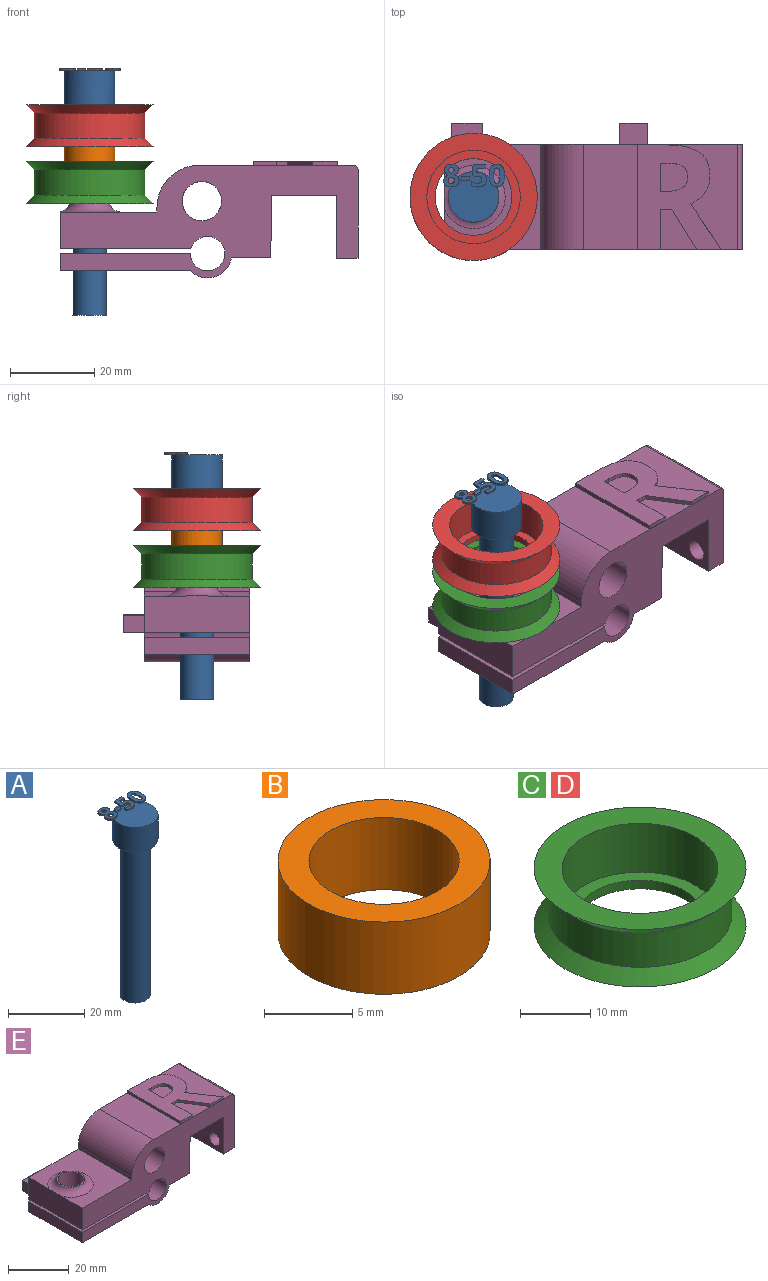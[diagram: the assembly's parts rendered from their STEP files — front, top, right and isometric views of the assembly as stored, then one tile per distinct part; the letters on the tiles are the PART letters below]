
ASSEMBLY  parts=5 mates=4
PART A: 86 faces, bbox 14.5x13.7x58.5 mm
  f0: plane 12x12mm, normal (0,0,1), area 99.4mm2, adj f5,f22,f23,f24,f25,f26,f40,f41
  f1: plane 1x0.26mm, normal (0,0,1), area 0.1mm2, adj f5,f46,f47,f48,f49
  f2: plane 0.85x0.68mm, normal (0,0,1), area 0.2mm2, adj f5,f29,f30,f31
  f3: cylinder r=4mm len=50mm, axis (0,0,-1), area 1256.6mm2, adj f4,f6
  f4: plane 8x8mm, normal (0,0,-1), area 50.3mm2, adj f3
  f5: cylinder r=6mm len=12mm, axis (0,0,-1), area 301.6mm2, adj f0,f1,f2,f6,f39,f45,f67,f85
  f6: plane 12x12mm, normal (0,0,-1), area 62.8mm2, adj f3,f5
  f7: extruded ~0.5x0.46mm, area 0.2mm2, adj f8,f37,f38,f39
  f8: extruded ~0.5x0.46mm, area 0.2mm2, adj f7,f9,f38,f39
  f9: extruded ~0.5x0.39mm, area 0.2mm2, adj f8,f10,f38,f39
  f10: extruded ~0.5x0.4mm, area 0.2mm2, adj f9,f11,f38,f39
  f11: extruded ~0.5x0.49mm, area 0.3mm2, adj f10,f12,f38,f39
  f12: extruded ~0.5x0.5mm, area 0.3mm2, adj f11,f13,f38,f39
  f13: extruded ~0.5x0.39mm, area 0.2mm2, adj f12,f37,f38,f39
  f14: extruded ~1.22x0.5mm, area 0.6mm2, adj f15,f35,f38,f39
  f15: extruded ~1.22x0.5mm, area 0.6mm2, adj f14,f16,f38,f39
  f16: extruded ~0.91x0.5mm, area 0.5mm2, adj f15,f17,f38,f39
  f17: extruded ~0.71x0.5mm, area 0.4mm2, adj f16,f18,f38,f39
  f18: extruded ~0.65x0.61mm, area 0.4mm2, adj f17,f19,f38,f39
  f19: extruded ~0.77x0.62mm, area 0.5mm2, adj f18,f20,f38,f39
  f20: extruded ~0.8x0.5mm, area 0.4mm2, adj f19,f21,f38,f39
  f21: extruded ~1.04x0.5mm, area 0.6mm2, adj f20,f22,f38,f39
  f22: extruded ~1.36x0.5mm, area 0.7mm2, adj f0,f21,f23,f38,f39
  f23: extruded ~1.33x0.5mm, area 0.7mm2, adj f0,f22,f24,f38
  f24: extruded ~1.04x0.51mm, area 0.6mm2, adj f0,f23,f25,f38
  f25: extruded ~0.75x0.5mm, area 0.4mm2, adj f0,f24,f26,f38
  f26: extruded ~0.85x0.66mm, area 0.5mm2, adj f0,f25,f27,f38,f39
  f27: extruded ~0.72x0.56mm, area 0.5mm2, adj f26,f28,f38,f39
  f28: extruded ~0.72x0.5mm, area 0.4mm2, adj f27,f35,f38,f39
  f29: extruded ~0.5x0.45mm, area 0.3mm2, adj f2,f30,f36,f38,f39
  f30: extruded ~0.5x0.47mm, area 0.3mm2, adj f2,f29,f31,f38
  f31: extruded ~0.62x0.5mm, area 0.3mm2, adj f2,f30,f32,f38,f39
  f32: extruded ~0.59x0.5mm, area 0.3mm2, adj f31,f33,f38,f39
  f33: extruded ~0.5x0.48mm, area 0.3mm2, adj f32,f34,f38,f39
  f34: extruded ~0.89x0.77mm, area 0.6mm2, adj f33,f36,f38,f39
  f35: extruded ~0.93x0.5mm, area 0.5mm2, adj f14,f28,f38,f39
  f36: extruded ~0.66x0.5mm, area 0.4mm2, adj f29,f34,f38,f39
  f37: extruded ~0.5x0.39mm, area 0.2mm2, adj f7,f13,f38,f39
  f38: plane 5.4x3.69mm, normal (0,0,1), area 12.7mm2, adj f7,f8,f9,f10,f11,f12,f13,f14
  f39: plane 5.4x3.53mm, normal (0,0,-1), area 10.2mm2, adj f5,f7,f8,f9,f10,f11,f12,f13
  f40: plane 0.9x0.5mm, normal (-1,0,0), area 0.4mm2, adj f0,f41,f43,f44
  f41: plane 1.93x0.5mm, normal (0,-1,0), area 1mm2, adj f0,f40,f42,f44
  f42: plane 0.9x0.5mm, normal (1,0,0), area 0.4mm2, adj f0,f41,f43,f44
  f43: plane 1.93x0.5mm, normal (0,1,0), area 1mm2, adj f0,f40,f42,f44
  f44: plane 1.93x0.9mm, normal (0,0,1), area 1.7mm2, adj f40,f41,f42,f43
  f45: plane 0.76x0.31mm, normal (0,0,-1), area 0mm2, adj f5,f46
  f46: extruded ~1.21x0.5mm, area 0.7mm2, adj f0,f1,f45,f47,f65,f66
  f47: extruded ~0.54x0.5mm, area 0.3mm2, adj f1,f46,f48,f66
  f48: plane 0.5x0.13mm, normal (-0.2,0.98,0), area 0.1mm2, adj f1,f47,f49,f66
  f49: plane 1.03x0.5mm, normal (1,-0.09,0), area 0.5mm2, adj f1,f48,f50,f66,f67
  f50: plane 1.88x0.5mm, normal (0,-1,0), area 0.9mm2, adj f49,f51,f66,f67
  f51: plane 0.94x0.5mm, normal (1,0,0), area 0.5mm2, adj f50,f52,f66,f67
  f52: plane 2.85x0.5mm, normal (0,1,0), area 1.4mm2, adj f51,f53,f66,f67
  f53: plane 2.68x0.5mm, normal (-1,0.07,0), area 1.3mm2, adj f0,f52,f54,f66,f67
  f54: plane 0.5x0.44mm, normal (-0.47,-0.88,0), area 0.3mm2, adj f0,f53,f55,f66
  f55: extruded ~0.5x0.37mm, area 0.2mm2, adj f0,f54,f56,f66
  f56: extruded ~0.5x0.42mm, area 0.2mm2, adj f0,f55,f57,f66
  f57: extruded ~1.05x0.8mm, area 0.8mm2, adj f0,f56,f58,f66
  f58: extruded ~1.02x0.83mm, area 0.8mm2, adj f0,f57,f59,f66
  f59: extruded ~0.72x0.5mm, area 0.4mm2, adj f0,f58,f60,f66
  f60: extruded ~0.66x0.5mm, area 0.4mm2, adj f0,f59,f61,f66
  f61: plane 0.96x0.5mm, normal (-1,0,0), area 0.5mm2, adj f0,f60,f62,f66
  f62: extruded ~1.42x0.5mm, area 0.7mm2, adj f0,f61,f63,f66
  f63: extruded ~1.55x0.5mm, area 0.8mm2, adj f0,f62,f64,f66
  f64: extruded ~1.36x0.54mm, area 0.8mm2, adj f0,f63,f65,f66
  f65: extruded ~1.17x0.5mm, area 0.6mm2, adj f0,f46,f64,f66
  f66: plane 5.33x3.51mm, normal (0,0,1), area 10.9mm2, adj f46,f47,f48,f49,f50,f51,f52,f53
  f67: plane 2.97x1.71mm, normal (0,0,-1), area 3.5mm2, adj f5,f49,f50,f51,f52,f53
  f68: extruded ~1.39x0.5mm, area 0.7mm2, adj f69,f83,f84,f85
  f69: extruded ~1.39x0.5mm, area 0.7mm2, adj f68,f70,f84,f85
  f70: extruded ~0.56x0.5mm, area 0.4mm2, adj f69,f71,f84,f85
  f71: extruded ~0.56x0.5mm, area 0.4mm2, adj f70,f72,f84,f85
  f72: extruded ~1.39x0.5mm, area 0.7mm2, adj f71,f73,f84,f85
  f73: extruded ~1.38x0.5mm, area 0.7mm2, adj f72,f74,f84,f85
  f74: extruded ~0.56x0.5mm, area 0.4mm2, adj f73,f83,f84,f85
  f75: extruded ~2.04x0.5mm, area 1.1mm2, adj f76,f82,f84,f85
  f76: extruded ~2.02x0.5mm, area 1.1mm2, adj f75,f77,f84,f85
  f77: extruded ~1.38x0.69mm, area 0.8mm2, adj f76,f78,f84,f85
  f78: extruded ~1.38x0.66mm, area 0.8mm2, adj f77,f79,f84,f85
  f79: extruded ~2.05x0.5mm, area 1.1mm2, adj f78,f80,f84,f85
  f80: extruded ~2.02x0.5mm, area 1mm2, adj f0,f79,f81,f84,f85
  f81: extruded ~1.37x0.68mm, area 0.8mm2, adj f0,f80,f82,f84
  f82: extruded ~1.39x0.66mm, area 0.8mm2, adj f0,f75,f81,f84,f85
  f83: extruded ~0.56x0.5mm, area 0.4mm2, adj f68,f74,f84,f85
  f84: plane 5.41x3.68mm, normal (0,0,1), area 12.1mm2, adj f68,f69,f70,f71,f72,f73,f74,f75
  f85: plane 5.41x3.68mm, normal (0,0,-1), area 10.3mm2, adj f5,f68,f69,f70,f71,f72,f73,f74
PART B: 4 faces, bbox 12x12x5 mm
  f0: cylinder r=4.25mm len=8.5mm, axis (0,0,-1), area 133.5mm2, adj f2,f3
  f1: cylinder r=6mm len=12mm, axis (0,0,-1), area 188.5mm2, adj f2,f3
  f2: plane 12x12mm, normal (0,0,1), area 56.4mm2, adj f0,f1
  f3: plane 12x12mm, normal (0,0,-1), area 56.4mm2, adj f0,f1
PART C: 8 faces, bbox 30.2x30.2x10 mm
  f0: plane 30.2x30.2mm, normal (0,0,1), area 329.2mm2, adj f1,f7
  f1: cylinder r=11.1mm len=22.2mm, axis (0,0,-1), area 592.8mm2, adj f0,f2
  f2: plane 22.2x22.2mm, normal (0,0,1), area 126.9mm2, adj f1,f3
  f3: cylinder r=9.1mm len=18.2mm, axis (0,0,-1), area 85.8mm2, adj f2,f4
  f4: plane 30.2x30.2mm, normal (0,0,-1), area 456.2mm2, adj f3,f5
  f5: cone r=13.1mm half-angle=45deg, axis (0,0,-1), area 250.6mm2, adj f4,f6
  f6: cylinder r=13.1mm len=26.2mm, axis (0,0,-1), area 493.9mm2, adj f5,f7
  f7: cone r=15.1mm half-angle=45deg, axis (0,0,1), area 250.6mm2, adj f0,f6
PART D: same geometry as C
PART E: 57 faces, bbox 74.2x30x27.7 mm
  f0: plane 25x4.12mm, normal (-1,0,0), area 103mm2, adj f3,f13,f14,f18
  f1: cylinder r=4.17mm len=8.35mm, axis (0,0,1), area 108.1mm2, adj f3,f18
  f2: plane 25x9.34mm, normal (0,0,-1), area 233.4mm2, adj f12,f13,f14,f16
  f3: plane 30.88x25mm, normal (0,0,-1), area 717.2mm2, adj f0,f1,f13,f14,f16
  f4: plane 25x8.82mm, normal (-1,0,0), area 219.6mm2, adj f5,f13,f14,f19,f23
  f5: plane 25x23mm, normal (0,0,1), area 400mm2, adj f4,f6,f13,f14,f23
  f6: plane 25x1.1mm, normal (-1,0,0), area 27.5mm2, adj f5,f13,f14,f24
  f7: plane 36.72x25mm, normal (0,0,1), area 579.3mm2, adj f13,f14,f24,f26,f36,f37,f38,f39
  f8: plane 25x21.09mm, normal (1,0,0), area 493.5mm2, adj f9,f13,f14,f21,f22,f26
  f9: plane 25x5mm, normal (0,0,-1), area 125mm2, adj f8,f10,f13,f14
  f10: plane 25x15mm, normal (-1,0,0), area 341.3mm2, adj f9,f11,f13,f14,f21,f22
  f11: plane 25x15.5mm, normal (0,0,-1), area 387.5mm2, adj f10,f12,f13,f14
  f12: plane 25x14.91mm, normal (1,0,-0.01), area 372.8mm2, adj f2,f11,f13,f14
  f13: plane 70.72x26.75mm, normal (0,-1,0), area 1024.3mm2, adj f0,f2,f3,f4,f5,f6,f7,f8
  f14: plane 70.72x26.75mm, normal (0,1,0), area 964.4mm2, adj f0,f2,f3,f4,f5,f6,f7,f8
  f15: cylinder r=4.17mm len=10.78mm, axis (0,0,1), area 282.8mm2, adj f19,f20
  f16: cylinder r=5.75mm len=25mm, axis (0,-1,0), area 315.9mm2, adj f2,f3,f13,f14
  f17: cylinder r=4.1mm len=25mm, axis (0,-1,0), area 618.7mm2, adj f13,f14,f18,f19
  f18: plane 30.91x25mm, normal (0,0,1), area 718.1mm2, adj f0,f1,f13,f14,f17
  f19: plane 31.07x30mm, normal (0,0,-1), area 758.4mm2, adj f4,f13,f14,f15,f17,f28,f29,f30
  f20: plane 9.35x9.35mm, normal (0,0,1), area 13.9mm2, adj f15,f23
  f21: cylinder r=2.43mm len=5mm, axis (1,0,0), area 76.2mm2, adj f8,f10
  f22: cylinder r=2.2mm len=5mm, axis (1,0,0), area 69.1mm2, adj f8,f10
  f23: torus R=7.5mm, axis (0,0,-1), area 134.6mm2, adj f4,f5,f20
  f24: cylinder r=10mm len=25mm, axis (0,-1,0), area 392.7mm2, adj f6,f7,f13,f14
  f25: cylinder r=4.68mm len=25mm, axis (0,-1,0), area 735.2mm2, adj f13,f14
  f26: cylinder r=1mm len=25mm, axis (0,-1,0), area 39.3mm2, adj f7,f8,f13,f14
  f27: plane 7.3x5mm, normal (0,0,1), area 36.5mm2, adj f14,f28,f29,f30
  f28: plane 5x4.12mm, normal (-1,0,0), area 20.6mm2, adj f14,f19,f27,f30
  f29: plane 5x4.12mm, normal (1,0,0), area 20.6mm2, adj f14,f19,f27,f30
  f30: plane 7.3x4.12mm, normal (0,1,0), area 30.1mm2, adj f19,f27,f28,f29
  f31: plane 6.63x5mm, normal (0,0,1), area 33.2mm2, adj f14,f32,f34,f35
  f32: plane 5x4.5mm, normal (-1,0,0), area 22.5mm2, adj f14,f31,f33,f35
  f33: plane 6.63x5mm, normal (0,0,-1), area 33.2mm2, adj f14,f32,f34,f35
  f34: plane 5x4.5mm, normal (1,0,0), area 22.5mm2, adj f14,f31,f33,f35
  f35: plane 6.63x4.5mm, normal (0,1,0), area 29.9mm2, adj f31,f32,f33,f34
  f36: plane 9.51x1mm, normal (1,0,0), area 9.5mm2, adj f7,f37,f54,f55
  f37: plane 2.79x1mm, normal (0,-1,0), area 2.8mm2, adj f7,f36,f38,f55
  f38: plane 9.51x5.92mm, normal (-0.85,-0.53,0), area 11.2mm2, adj f7,f37,f39,f55
  f39: plane 5.83x1mm, normal (0,-1,0), area 5.8mm2, adj f7,f38,f40,f55
  f40: extruded ~10.8x7.29mm, area 13mm2, adj f7,f39,f41,f55
  f41: extruded ~3.41x2.67mm, area 4.4mm2, adj f7,f40,f42,f55
  f42: extruded ~3.89x1.2mm, area 4.1mm2, adj f7,f41,f43,f55
  f43: extruded ~5.59x2.42mm, area 6.3mm2, adj f7,f42,f44,f55
  f44: extruded ~7.48x1.84mm, area 7.8mm2, adj f7,f43,f45,f55
  f45: plane 7.22x1mm, normal (0,1,0), area 7.2mm2, adj f7,f44,f46,f55
  f46: plane 24.79x1mm, normal (-1,0,0), area 24.8mm2, adj f7,f45,f54,f55
  f47: plane 1.69x1mm, normal (0,1,0), area 1.7mm2, adj f48,f53,f55,f56
  f48: plane 6.7x1mm, normal (1,0,0), area 6.7mm2, adj f47,f49,f55,f56
  f49: plane 1.6x1mm, normal (0,-1,0), area 1.6mm2, adj f48,f50,f55,f56
  f50: extruded ~3.75x1mm, area 3.9mm2, adj f49,f51,f55,f56
  f51: extruded ~2.51x1.21mm, area 2.9mm2, adj f50,f52,f55,f56
  f52: extruded ~2.61x1.19mm, area 3mm2, adj f51,f53,f55,f56
  f53: extruded ~3.68x1mm, area 3.8mm2, adj f47,f52,f55,f56
  f54: plane 5.26x1mm, normal (0,-1,0), area 5.3mm2, adj f7,f36,f46,f55
  f55: plane 24.79x19.8mm, normal (0,0,1), area 300mm2, adj f36,f37,f38,f39,f40,f41,f42,f43
  f56: plane 6.7x6.56mm, normal (0,0,1), area 38.8mm2, adj f47,f48,f49,f50,f51,f52,f53
PLACE A t=(-103.78,-12.5,-13.6)mm
PLACE B rot(axis=(1,0,0),180deg) t=(-103.78,-12.5,26.4)mm
PLACE C t=(-103.78,-12.5,18.1)mm
PLACE D t=(-103.78,-12.5,31.6)mm
PLACE E t=(20,0,0)mm
MATE fastened A.f3 <-> D.f1  axis (0,0,-1) through (-103.78,-12.5,36.4)mm
MATE fastened B.f0 <-> C.f1  axis (0,0,1) through (-103.78,-12.5,21.4)mm
MATE fastened C.f1 <-> E.f1  axis (0,0,-1) through (-103.78,-12.5,12.9)mm
MATE fastened D.f1 <-> B.f0  axis (0,0,-1) through (-103.78,-12.5,26.4)mm
